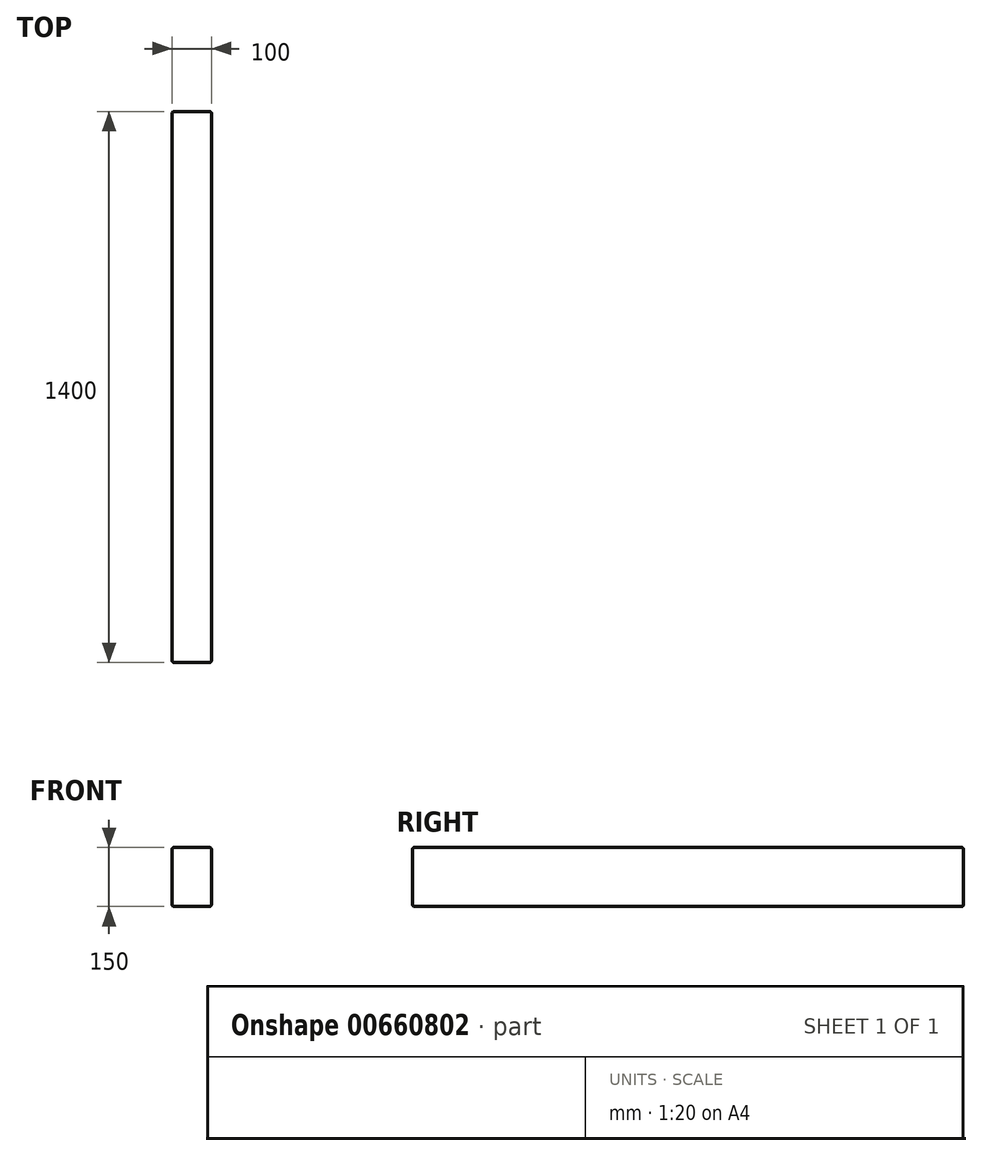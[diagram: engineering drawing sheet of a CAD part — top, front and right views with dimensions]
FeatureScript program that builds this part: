
annotation { "Feature Type Name" : "Feature", "Feature Type Description" : "" }
export const myFeature = defineFeature(function(context is Context, id is Id, definition is map)
    precondition{}
    {
        {
            var Q0;
            Q0=qCreatedBy(makeId("Top.planeOp"),FACE);
            var sketch = newSketch(context, id + "F0", { "sketchPlane" : qUnion([Q0])});
            skLineSegment(sketch, "E0.bottom", {"start": v(50, 700) * mm, "end": v(-50, 700) * mm});
            skLineSegment(sketch, "E0.top", {"start": v(50, -700) * mm, "end": v(-50, -700) * mm});
            skLineSegment(sketch, "E0.left", {"start": v(50, 700) * mm, "end": v(50, -700) * mm});
            skLineSegment(sketch, "E0.right", {"start": v(-50, 700) * mm, "end": v(-50, -700) * mm});
            skPoint(sketch, "E0.middle", {"position": v(0, 0) * mm});
            skSolve(sketch);
        }
        {
            var Q0;
            Q0 = qSketchRegion(id + "F0", true);
            extrude(context, id + "F1", {"entities" : qUnion([Q0]), "depth" : 150 * mm, "offsetDistance" : 25 * mm});
        }
        {
            var Q0;
            Q0=makeQuery(id+"F1.opExtrude","CAP_FACE",FACE,{"disambiguationData":[OSD([sQuery(id+"F0.wireOp",EDGE,"E0.bottom"),sQuery(id+"F0.wireOp",EDGE,"E0.top"),sQuery(id+"F0.wireOp",EDGE,"E0.left"),sQuery(id+"F0.wireOp",EDGE,"E0.right")])],"isStart":false});
            var Q1;
            Q1=makeQuery(id+"F1.opExtrude","SWEPT_FACE",FACE,{"disambiguationData":[OSD([sQuery(id+"F0.wireOp",EDGE,"E0.left")])]});
            var Q2;
            Q2=makeQuery(id+"F1.opExtrude","SWEPT_FACE",FACE,{"disambiguationData":[OSD([sQuery(id+"F0.wireOp",EDGE,"E0.top")])]});
            var Q3;
            Q3=makeQuery(id+"F1.opExtrude","SWEPT_FACE",FACE,{"disambiguationData":[OSD([sQuery(id+"F0.wireOp",EDGE,"E0.right")])]});
            var Q4;
            Q4=makeQuery(id+"F1.opExtrude","CAP_FACE",FACE,{"disambiguationData":[OSD([sQuery(id+"F0.wireOp",EDGE,"E0.bottom"),sQuery(id+"F0.wireOp",EDGE,"E0.top"),sQuery(id+"F0.wireOp",EDGE,"E0.left"),sQuery(id+"F0.wireOp",EDGE,"E0.right")])],"isStart":true});
            fillet(context, id + "F2", {"entities" : qUnion([Q0, Q1, Q2, Q3, Q4]), "radius" : 5 * mm, "tangentPropagation" : true, "allowEdgeOverflow" : false});
        }
    });
